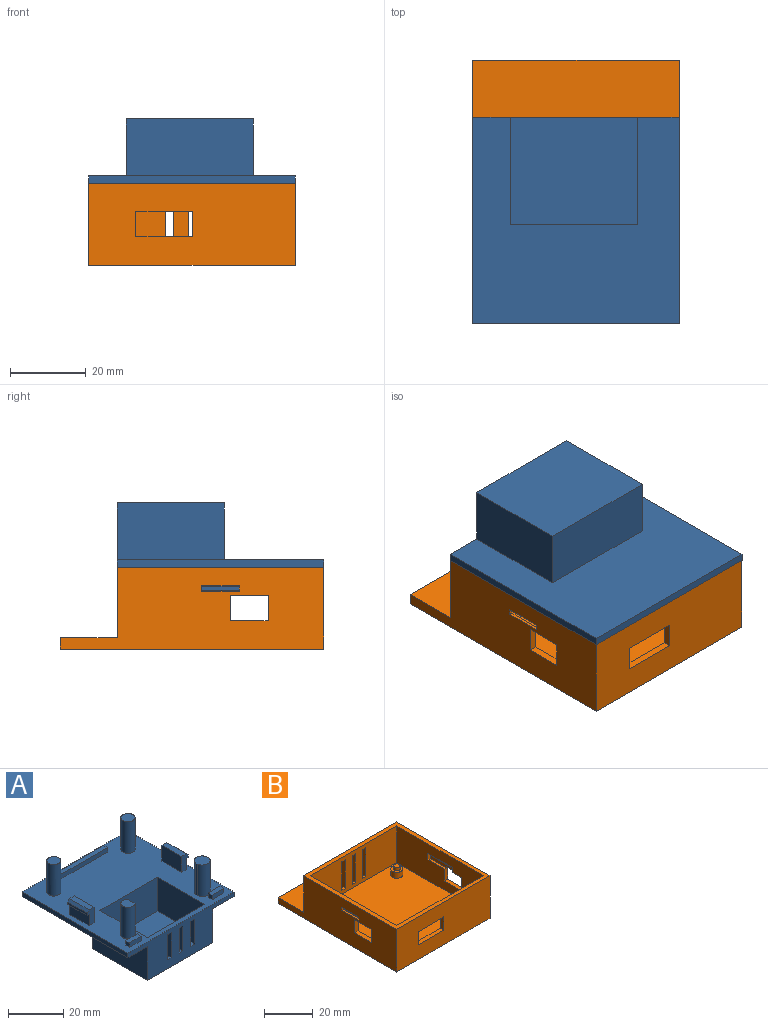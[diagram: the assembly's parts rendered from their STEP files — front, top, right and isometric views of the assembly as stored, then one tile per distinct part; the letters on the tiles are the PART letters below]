
ASSEMBLY  parts=2 mates=1
PART A: 68 faces, bbox 54.3x54.3x31 mm
  f0: plane 54.32x54.32mm, normal (0,0,1), area 2027.7mm2, adj f1,f2,f3,f4,f5,f8,f9,f10
  f1: plane 29.5x15mm, normal (0,1,0), area 376.5mm2, adj f0,f3,f5,f6,f15,f16,f17,f18
  f2: plane 54.32x17mm, normal (0,-1,0), area 545.1mm2, adj f0,f7,f8,f9,f11,f12,f13,f15
  f3: plane 24.2x15mm, normal (1,0,0), area 363mm2, adj f0,f1,f4,f6
  f4: plane 29.5x15mm, normal (0,-1,0), area 442.5mm2, adj f0,f3,f5,f6
  f5: plane 24.2x15mm, normal (-1,0,0), area 363mm2, adj f0,f1,f4,f6
  f6: plane 29.5x24.2mm, normal (0,0,1), area 713.8mm2, adj f1,f3,f4,f5
  f7: plane 54.32x54.32mm, normal (0,0,-1), area 2006mm2, adj f2,f8,f9,f10,f12,f13,f14
  f8: plane 54.32x2mm, normal (-1,0,0), area 108.6mm2, adj f0,f2,f7,f10
  f9: plane 54.32x2mm, normal (1,0,0), area 108.6mm2, adj f0,f2,f7,f10
  f10: plane 54.32x2mm, normal (0,1,0), area 108.6mm2, adj f0,f7,f8,f9
  f11: plane 33.5x28.2mm, normal (0,0,-1), area 944.6mm2, adj f2,f12,f13,f14
  f12: plane 28.2x15mm, normal (1,0,0), area 423mm2, adj f2,f7,f11,f14
  f13: plane 28.2x15mm, normal (-1,0,0), area 423mm2, adj f2,f7,f11,f14
  f14: plane 33.5x15mm, normal (0,1,0), area 502.5mm2, adj f7,f11,f12,f13
  f15: plane 2x2mm, normal (0,0,-1), area 4mm2, adj f1,f2,f16,f18
  f16: plane 11x2mm, normal (1,0,0), area 22mm2, adj f1,f2,f15,f17
  f17: plane 2x2mm, normal (0,0,1), area 4mm2, adj f1,f2,f16,f18
  f18: plane 11x2mm, normal (-1,0,0), area 22mm2, adj f1,f2,f15,f17
  f19: plane 2x2mm, normal (0,0,-1), area 4mm2, adj f1,f2,f20,f22
  f20: plane 11x2mm, normal (1,0,0), area 22mm2, adj f1,f2,f19,f21
  f21: plane 2x2mm, normal (0,0,1), area 4mm2, adj f1,f2,f20,f22
  f22: plane 11x2mm, normal (-1,0,0), area 22mm2, adj f1,f2,f19,f21
  f23: plane 2x2mm, normal (0,0,-1), area 4mm2, adj f1,f2,f24,f26
  f24: plane 11x2mm, normal (1,0,0), area 22mm2, adj f1,f2,f23,f25
  f25: plane 2x2mm, normal (0,0,1), area 4mm2, adj f1,f2,f24,f26
  f26: plane 11x2mm, normal (-1,0,0), area 22mm2, adj f1,f2,f23,f25
  f27: plane 5.06x5.06mm, normal (0,0,1), area 20.1mm2, adj f28
  f28: cylinder r=2.53mm len=13.99mm, axis (0,0,-1), area 222.3mm2, adj f0,f27
  f29: plane 5.13x4.23mm, normal (0,0,1), area 18.2mm2, adj f30,f31
  f30: plane 13.99x3.92mm, normal (1,0,0), area 54.8mm2, adj f0,f29,f31
  f31: cylinder r=2.57mm len=13.99mm, axis (0,0,-1), area 163.3mm2, adj f0,f29,f30
  f32: plane 5.74x5.71mm, normal (0,0,1), area 25.8mm2, adj f33,f34
  f33: plane 13.99x0.8mm, normal (-1,0,0), area 11.2mm2, adj f0,f32,f34
  f34: cylinder r=2.87mm len=13.99mm, axis (0,0,-1), area 240.9mm2, adj f0,f32,f33
  f35: plane 5.17x5.17mm, normal (0,0,1), area 21mm2, adj f36
  f36: cylinder r=2.58mm len=13.99mm, axis (0,0,-1), area 227.2mm2, adj f0,f35
  f37: plane 10x5mm, normal (-1,0,0), area 50mm2, adj f0,f38,f43,f44
  f38: plane 10x1mm, normal (0,0,-1), area 10mm2, adj f37,f39,f43,f44
  f39: plane 10x1mm, normal (-1,0,0), area 10mm2, adj f38,f40,f43,f44
  f40: plane 10x1mm, normal (-0.71,0,0.71), area 14.1mm2, adj f39,f41,f43,f44
  f41: plane 10x2.5mm, normal (0,0,1), area 25mm2, adj f40,f42,f43,f44
  f42: plane 10x7mm, normal (1,0,0), area 70mm2, adj f0,f41,f43,f44
  f43: plane 7x3.5mm, normal (0,1,0), area 19mm2, adj f0,f37,f38,f39,f40,f41,f42
  f44: plane 7x3.5mm, normal (0,-1,0), area 19mm2, adj f0,f37,f38,f39,f40,f41,f42
  f45: plane 10x7mm, normal (-1,0,0), area 70mm2, adj f0,f46,f51,f52
  f46: plane 10x2.5mm, normal (0,0,1), area 25mm2, adj f45,f47,f51,f52
  f47: plane 10x1mm, normal (0.71,0,0.71), area 14.1mm2, adj f46,f48,f51,f52
  f48: plane 10x1mm, normal (1,0,0), area 10mm2, adj f47,f49,f51,f52
  f49: plane 10x1mm, normal (0,0,-1), area 10mm2, adj f48,f50,f51,f52
  f50: plane 10x5mm, normal (1,0,0), area 50mm2, adj f0,f49,f51,f52
  f51: plane 7x3.5mm, normal (0,1,0), area 19mm2, adj f0,f45,f46,f47,f48,f49,f50
  f52: plane 7x3.5mm, normal (0,-1,0), area 19mm2, adj f0,f45,f46,f47,f48,f49,f50
  f53: plane 25x2mm, normal (0,1,0), area 50mm2, adj f0,f54,f56,f57
  f54: plane 2x2mm, normal (-1,0,0), area 4mm2, adj f0,f53,f55,f57
  f55: plane 25x2mm, normal (0,-1,0), area 50mm2, adj f0,f54,f56,f57
  f56: plane 2x2mm, normal (1,0,0), area 4mm2, adj f0,f53,f55,f57
  f57: plane 25x2mm, normal (0,0,1), area 50mm2, adj f53,f54,f55,f56
  f58: plane 6x2mm, normal (0,1,0), area 12mm2, adj f0,f59,f61,f62
  f59: plane 2x2mm, normal (-1,0,0), area 4mm2, adj f0,f58,f60,f62
  f60: plane 6x2mm, normal (0,-1,0), area 12mm2, adj f0,f59,f61,f62
  f61: plane 2x2mm, normal (1,0,0), area 4mm2, adj f0,f58,f60,f62
  f62: plane 6x2mm, normal (0,0,1), area 12mm2, adj f58,f59,f60,f61
  f63: plane 6x2mm, normal (0,1,0), area 12mm2, adj f0,f64,f66,f67
  f64: plane 2x2mm, normal (-1,0,0), area 4mm2, adj f0,f63,f65,f67
  f65: plane 6x2mm, normal (0,-1,0), area 12mm2, adj f0,f64,f66,f67
  f66: plane 2x2mm, normal (1,0,0), area 4mm2, adj f0,f63,f65,f67
  f67: plane 6x2mm, normal (0,0,1), area 12mm2, adj f63,f64,f65,f66
PART B: 69 faces, bbox 54.3x69.3x21.5 mm
  f0: plane 69.32x21.5mm, normal (1,0,0), area 1131.4mm2, adj f6,f11,f12,f13,f14,f15,f37,f38
  f1: plane 69.32x21.5mm, normal (-1,0,0), area 1131.4mm2, adj f4,f5,f6,f11,f12,f13,f14,f15
  f2: plane 14x3.2mm, normal (1,0,0), area 26.9mm2, adj f4,f5,f55,f56,f57,f58,f66,f67
  f3: plane 14x3.2mm, normal (-1,0,0), area 26.9mm2, adj f37,f40,f59,f60,f61,f62,f63,f64
  f4: plane 6.65x2mm, normal (0,-1,0), area 12.5mm2, adj f1,f2,f5,f8,f41,f55
  f5: plane 10x2mm, normal (0,0,-1), area 14.6mm2, adj f1,f2,f4,f8,f42,f57
  f6: plane 54.32x21.5mm, normal (0,-1,0), area 1068.1mm2, adj f0,f1,f14,f15,f43,f44,f45,f46
  f7: plane 50.32x18.5mm, normal (0,1,0), area 831.2mm2, adj f8,f9,f15,f16,f43,f44,f45,f46
  f8: plane 50.32x18.5mm, normal (1,0,0), area 822.6mm2, adj f4,f5,f7,f10,f15,f16,f41,f42
  f9: plane 50.32x18.5mm, normal (-1,0,0), area 822.6mm2, adj f7,f10,f15,f16,f37,f38,f39,f40
  f10: plane 50.32x18.5mm, normal (0,-1,0), area 843.9mm2, adj f8,f9,f15,f16,f25,f26,f27,f28
  f11: plane 54.32x18.5mm, normal (0,1,0), area 917.9mm2, adj f0,f1,f12,f15,f25,f26,f27,f28
  f12: plane 54.32x15mm, normal (0,0,1), area 814.8mm2, adj f0,f1,f11,f13
  f13: plane 54.32x3mm, normal (0,1,0), area 163mm2, adj f0,f1,f12,f14
  f14: plane 69.32x54.32mm, normal (0,0,-1), area 3765.5mm2, adj f0,f1,f6,f13
  f15: plane 54.32x54.32mm, normal (0,0,1), area 418.6mm2, adj f0,f1,f6,f7,f8,f9,f10,f11
  f16: plane 50.32x50.32mm, normal (0,0,1), area 2453.6mm2, adj f7,f8,f9,f10,f17,f19,f21,f23
  f17: cylinder r=2.5mm len=5mm, axis (0,0,-1), area 47.1mm2, adj f16,f18
  f18: plane 5x5mm, normal (0,0,1), area 13.5mm2, adj f17,f47
  f19: cylinder r=2.5mm len=5mm, axis (0,0,-1), area 47.1mm2, adj f16,f20
  f20: plane 5x5mm, normal (0,0,1), area 13.5mm2, adj f19,f49
  f21: cylinder r=2.5mm len=5mm, axis (0,0,-1), area 47.1mm2, adj f16,f22
  f22: plane 5x5mm, normal (0,0,1), area 13.5mm2, adj f21,f51
  f23: cylinder r=2.5mm len=5mm, axis (0,0,-1), area 47.1mm2, adj f16,f24
  f24: plane 5x5mm, normal (0,0,1), area 13.5mm2, adj f23,f53
  f25: plane 2x2mm, normal (0,0,-1), area 4mm2, adj f10,f11,f26,f28
  f26: plane 14.5x2mm, normal (-1,0,0), area 29mm2, adj f10,f11,f25,f27
  f27: plane 2x2mm, normal (0,0,1), area 4mm2, adj f10,f11,f26,f28
  f28: plane 14.5x2mm, normal (1,0,0), area 29mm2, adj f10,f11,f25,f27
  f29: plane 2x2mm, normal (0,0,-1), area 4mm2, adj f10,f11,f30,f32
  f30: plane 14.5x2mm, normal (-1,0,0), area 29mm2, adj f10,f11,f29,f31
  f31: plane 2x2mm, normal (0,0,1), area 4mm2, adj f10,f11,f30,f32
  f32: plane 14.5x2mm, normal (1,0,0), area 29mm2, adj f10,f11,f29,f31
  f33: plane 2x2mm, normal (0,0,-1), area 4mm2, adj f10,f11,f34,f36
  f34: plane 14.5x2mm, normal (-1,0,0), area 29mm2, adj f10,f11,f33,f35
  f35: plane 2x2mm, normal (0,0,1), area 4mm2, adj f10,f11,f34,f36
  f36: plane 14.5x2mm, normal (1,0,0), area 29mm2, adj f10,f11,f33,f35
  f37: plane 10x2mm, normal (0,0,-1), area 14.6mm2, adj f0,f3,f9,f38,f40,f61
  f38: plane 6.65x2mm, normal (0,1,0), area 13.3mm2, adj f0,f9,f37,f39
  f39: plane 10x2mm, normal (0,0,1), area 20mm2, adj f0,f9,f38,f40
  f40: plane 6.65x2mm, normal (0,-1,0), area 12.5mm2, adj f0,f3,f9,f37,f39,f59
  f41: plane 10x2mm, normal (0,0,1), area 20mm2, adj f1,f4,f8,f42
  f42: plane 6.65x2mm, normal (0,1,0), area 13.3mm2, adj f1,f5,f8,f41
  f43: plane 15x2mm, normal (0,0,-1), area 30mm2, adj f6,f7,f44,f46
  f44: plane 6.65x2mm, normal (1,0,0), area 13.3mm2, adj f6,f7,f43,f45
  f45: plane 15x2mm, normal (0,0,1), area 30mm2, adj f6,f7,f44,f46
  f46: plane 6.65x2mm, normal (-1,0,0), area 13.3mm2, adj f6,f7,f43,f45
  f47: cylinder r=1.4mm len=2.8mm, axis (0,0,-1), area 13.2mm2, adj f18,f48
  f48: plane 2.8x2.8mm, normal (0,0,1), area 6.2mm2, adj f47
  f49: cylinder r=1.4mm len=2.8mm, axis (0,0,-1), area 13.2mm2, adj f20,f50
  f50: plane 2.8x2.8mm, normal (0,0,1), area 6.2mm2, adj f49
  f51: cylinder r=1.4mm len=2.8mm, axis (0,0,-1), area 13.2mm2, adj f22,f52
  f52: plane 2.8x2.8mm, normal (0,0,1), area 6.2mm2, adj f51
  f53: cylinder r=1.4mm len=2.8mm, axis (0,0,-1), area 13.2mm2, adj f24,f54
  f54: plane 2.8x2.8mm, normal (0,0,1), area 6.2mm2, adj f53
  f55: plane 9.54x1.2mm, normal (0,0,1), area 11.4mm2, adj f2,f4,f8,f58
  f56: plane 14x2mm, normal (0,0,-1), area 24.8mm2, adj f1,f2,f8,f57,f58,f67,f68
  f57: plane 2.54x1.2mm, normal (0,1,0), area 3mm2, adj f2,f5,f8,f56
  f58: plane 3.2x1.2mm, normal (0,-1,0), area 3.8mm2, adj f2,f8,f55,f56
  f59: plane 9.54x1.2mm, normal (0,0,1), area 11.4mm2, adj f3,f9,f40,f62
  f60: plane 14x2mm, normal (0,0,-1), area 24.8mm2, adj f0,f3,f9,f61,f62,f64,f65
  f61: plane 2.54x1.2mm, normal (0,1,0), area 3mm2, adj f3,f9,f37,f60
  f62: plane 3.2x1.2mm, normal (0,-1,0), area 3.8mm2, adj f3,f9,f59,f60
  f63: plane 10x0.8mm, normal (0,0,1), area 8mm2, adj f0,f3,f64,f65
  f64: plane 1.5x0.8mm, normal (0,1,0), area 1.2mm2, adj f0,f3,f60,f63
  f65: plane 1.5x0.8mm, normal (0,-1,0), area 1.2mm2, adj f0,f3,f60,f63
  f66: plane 10x0.8mm, normal (0,0,1), area 8mm2, adj f1,f2,f67,f68
  f67: plane 1.5x0.8mm, normal (0,1,0), area 1.2mm2, adj f1,f2,f56,f66
  f68: plane 1.5x0.8mm, normal (0,-1,0), area 1.2mm2, adj f1,f2,f56,f66
PLACE A rot(axis=(1,0,0),180deg) t=(-37,-5.68,44.51)mm
PLACE B t=(-30.28,-5.71,11.01)mm
MATE fastened A.f0 <-> B.f15  axis (0,0,-1) through (-6.67,18.97,29.51)mm
